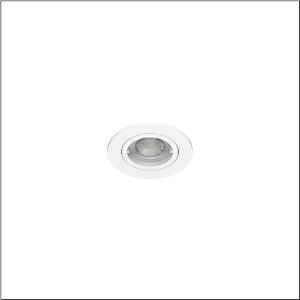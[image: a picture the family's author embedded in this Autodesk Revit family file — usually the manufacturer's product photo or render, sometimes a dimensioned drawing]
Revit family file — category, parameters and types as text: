
# Revit family: lunis_41_spot_51dt137a41a
name_source: partatom
category: Lighting Fixtures
units: mm (PartAtom-declared; Revit-internal decimal feet)

## family parameters
Cut with Voids When Loaded = No
Host = Face
Light Source = No
Part Type = Normal
Room Calculation Point = No
Round Connector Dimension = Use Diameter
Shared = No

## types (1)
- Lunis 41 Spot (1 x LED, 550 lm, 5 W, 4000K)
    Apparent Load = 5 VA
    CIE Flux Codes = 87 97 99 100 100
    Color Rendering = 80
    Color Temperature = 4000K
    Default Elevation = 1800 mm
    Description = Lunis 41,  Spot, downlight, light emission: direct distribution, LED rated luminous flux: 550lm, light colour: 840, control gear: ECG, mains connection: 230V, AC, 50/60Hz, housing, round, of aluminium, coated, traffic white (RAL 9016), diameter: 88mm, recess depth: 54mm, protection rating (complete): IP20, protection rating (on room side): IP20, insulation class (complete): insulation class II (safety insulation), certification: CE, permissible ambient temperature for indoor applications: -20..+40°C, packaging unit: 1 piece
    Height = 0 mm  [stored 0 ft]
    Lamp = 1 x LED
    Lamp Light Flux = 550 lm
    Lamp Power = 5 W
    Lamp count = 1
    Length = 88 mm
    Luminous efficacy = 110 lm/W
    Manufacturer = Siteco
    ModVariant = No
    Model = 51DT137A41A
    Mounting Place = Ceiling
    Mounting Type = Recessed
    Number of Poles = 1
    OnlyDefault = Yes
    Power Factor = 1
    Product Name = Lunis 41 Spot
    Product group = downlight
    ProductGroupID = 400
    Protection Class = Protection class II
    Protection Degree = IP 20
    RLX_Detail_Level = 1
    RLX_Emergency_Light_Flux = 0 lm
    RLX_Emergency_Type = 0
    RLX_Emergency_Type_DB = No
    RlxData = <blob elided: 37997 chars, md5=f92c5618>
    Socket = socket
    Standby Power = 0 W
    System Light Flux = 550 lm
    System Power = 5 W
    Type Comments = Product without accessories
    Type Image = l_1005286.jpg
    URL = http://relux.com
    VarID = ---
    Voltage = 0 V
    Weight = 0.00 kg
    Width = 0 mm  [stored 0 ft]

note: [stored X ft] marks values corroborated as IEEE doubles in the binary element streams (Revit-internal decimal feet)

## geometry (parser evidence)
native form markers: Blend x4, Sweep x8
no freeform markers — native parametric forms only
